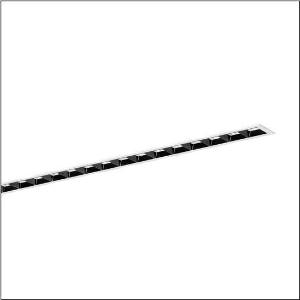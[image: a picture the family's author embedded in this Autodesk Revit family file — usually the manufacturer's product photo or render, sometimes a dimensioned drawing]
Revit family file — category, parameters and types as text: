
# Revit family: silica_r__21_51mx14dc3awb_1e66
name_source: partatom
category: Lighting Fixtures
units: mm (PartAtom-declared; Revit-internal decimal feet)

## family parameters
Cut with Voids When Loaded = No
Host = Face
Light Source = No
Part Type = Normal
Room Calculation Point = No
Round Connector Dimension = Use Diameter
Shared = No

## types (1)
- --- (1 x LED, 10800 lm, 79 W, 3000K)
    Apparent Load = 79 VA
    CIE Flux Codes = 74 94 99 100 100
    Color Rendering = 80
    Color Temperature = 3000K
    Default Elevation = 1800 mm
    Description = Silica® 21, office luminaire, primary light control with darklight reflector, of PMMA, black, light emission: direct distribution, primary light characteristic: asymmetric, installation type: recessed, LED, rated luminous flux: 10.800lm, luminous efficacy: 137lm/W, light colour: 830, colour temperature: 3000K, with terminal, 3+2-pole, max. 2.5mm², mains connection: 220..240V, AC, 50/60Hz, rated input power: 79W, luminaire housing, of aluminium, traffic white (RAL 9016), length: 3.028mm, width: 79mm, height: 53mm, protection rating (complete): IP20, insulation class (complete): insulation class I (protective earthing), certification: CE, permissible operating ambient temperature: 0..+35°C, standard: EN 50419, packaging unit: 1 piece
    Height = 0 mm  [stored 0 ft]
    Lamp = 1 x LED
    Lamp Light Flux = 10800 lm
    Lamp Power = 79 W
    Lamp count = 1
    Length = 3027 mm
    Luminous efficacy = 137 lm/W
    Manufacturer = Siteco
    ModVariant = No
    Model = 51MX14DC3AWB
    Mounting Place = Ceiling
    Mounting Type = Recessed
    Number of Poles = 1
    OnlyDefault = Yes
    Power Factor = 1
    Product Name = Silica® 21
    Product group = office luminaire | ceiling recessed
    ProductGroupID = 401
    Protection Class = Protection class I
    Protection Degree = IP 20
    RLX_Detail_Level = 1
    RLX_Emergency_Light_Flux = 0 lm
    RLX_Emergency_Type = 0
    RLX_Emergency_Type_DB = No
    RlxData = <blob elided: 63209 chars, md5=99dd8e65>
    Socket = socket
    Standby Power = 0 W
    System Light Flux = 10800 lm
    System Power = 79 W
    Type Comments = factory setting: luminous flux: 100 % | dim-lin: 254 | 448 mA
    Type Image = l_1297791.jpg
    URL = http://relux.com
    VarID = @adj_053015
    Voltage = 0 V
    Weight = 0.00 kg
    Width = 79 mm

note: [stored X ft] marks values corroborated as IEEE doubles in the binary element streams (Revit-internal decimal feet)

## geometry (parser evidence)
native form markers: Blend x4, Sweep x9
no freeform markers — native parametric forms only
